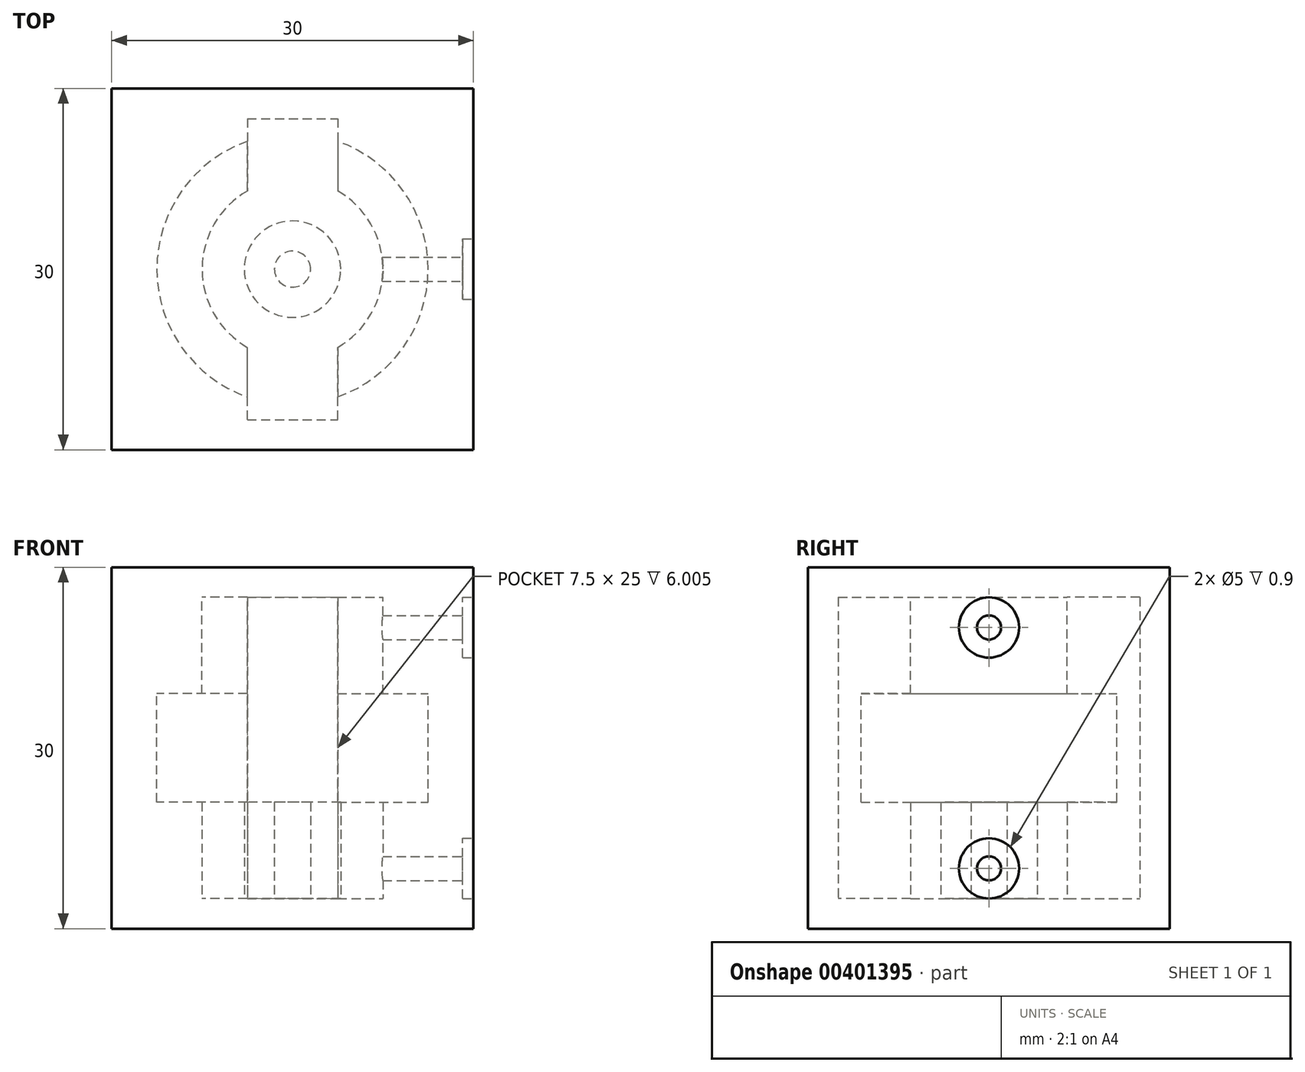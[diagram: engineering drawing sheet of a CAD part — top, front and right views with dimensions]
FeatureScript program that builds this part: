
annotation { "Feature Type Name" : "Feature", "Feature Type Description" : "" }
export const myFeature = defineFeature(function(context is Context, id is Id, definition is map)
    precondition{}
    {
        {
            var Q0;
            Q0=qCreatedBy(makeId("Top.planeOp"),FACE);
            var sketch = newSketch(context, id + "F0", { "sketchPlane" : qUnion([Q0])});
            skLineSegment(sketch, "E0.bottom", {"start": v(-15, 15) * mm, "end": v(15, 15) * mm});
            skLineSegment(sketch, "E0.top", {"start": v(-15, -15) * mm, "end": v(15, -15) * mm});
            skLineSegment(sketch, "E0.left", {"start": v(-15, 15) * mm, "end": v(-15, -15) * mm});
            skLineSegment(sketch, "E0.right", {"start": v(15, 15) * mm, "end": v(15, -15) * mm});
            skSolve(sketch);
        }
        {
            var Q0;
            Q0 = qSketchRegion(id + "F0", true);
            extrude(context, id + "F1", {"entities" : qUnion([Q0]), "depth" : 30 * mm});
        }
        {
            var Q0;
            Q0=makeQuery(id+"F1.opExtrude","CAP_FACE",FACE,{"disambiguationData":[OSD([sQuery(id+"F0.wireOp",EDGE,"E0.bottom"),sQuery(id+"F0.wireOp",EDGE,"E0.top"),sQuery(id+"F0.wireOp",EDGE,"E0.left"),sQuery(id+"F0.wireOp",EDGE,"E0.right")])],"isStart":false});
            var Q1;
            Q1=makeQuery(id+"F1.opExtrude","SWEPT_BODY",BODY,{"disambiguationData":[OSD([sQuery(id+"F0.wireOp",EDGE,"E0.bottom"),sQuery(id+"F0.wireOp",EDGE,"E0.top"),sQuery(id+"F0.wireOp",EDGE,"E0.left"),sQuery(id+"F0.wireOp",EDGE,"E0.right")])]});
            shell(context, id + "F2", {"isHollow" : true, "entities" : qUnion([Q0]), "parts" : qUnion([Q1]), "thickness" : 2.5 * mm});
        }
        {
            var Q0;
            Q0=qCreatedBy(makeId("Top.planeOp"),FACE);
            var sketch = newSketch(context, id + "F3", { "sketchPlane" : qUnion([Q0])});
            skArc(sketch, "E1", {"start": v(7.5, 0) * mm, "mid": v(6.5, 3.75) * mm, "end": v(3.75, 6.5) * mm});
            skLineSegment(sketch, "E2", {"start": v(3.75, 12.5) * mm, "end": v(3.75, 6.5) * mm});
            skLineSegment(sketch, "E3", {"start": v(-3.75, 12.5) * mm, "end": v(-3.75, 6.5) * mm});
            skArc(sketch, "E4.trimOffspring", {"start": v(-3.75, 6.5) * mm, "mid": v(-6.5, 3.75) * mm, "end": v(-7.5, 0) * mm});
            skArc(sketch, "E5.MirrorCS", {"start": v(-3.75, -6.5) * mm, "mid": v(-6.5, -3.75) * mm, "end": v(-7.5, 0) * mm});
            skLineSegment(sketch, "E6.MirrorCS", {"start": v(-3.75, -12.5) * mm, "end": v(-3.75, -6.5) * mm});
            skLineSegment(sketch, "E7.MirrorCS", {"start": v(3.75, -12.5) * mm, "end": v(3.75, -6.5) * mm});
            skArc(sketch, "E8.MirrorCS", {"start": v(7.5, 0) * mm, "mid": v(6.5, -3.75) * mm, "end": v(3.75, -6.5) * mm});
            skPoint(sketch, "E9.MirrorCS.end.orphan", {"position": v(3.75, -12.5) * mm});
            skPoint(sketch, "E9.MirrorCS.start.orphan", {"position": v(-3.75, -12.5) * mm});
            skLineSegment(sketch, "E10.0", {"start": v(-12.5, 12.5) * mm, "end": v(-12.5, -12.5) * mm});
            skLineSegment(sketch, "E11", {"start": v(-12.5, 12.5) * mm, "end": v(-3.75, 12.5) * mm});
            skLineSegment(sketch, "E12", {"start": v(-12.5, -12.5) * mm, "end": v(-3.75, -12.5) * mm});
            skLineSegment(sketch, "E13.0", {"start": v(12.5, 12.5) * mm, "end": v(12.5, -12.5) * mm});
            skLineSegment(sketch, "E14", {"start": v(12.5, 12.5) * mm, "end": v(3.75, 12.5) * mm});
            skLineSegment(sketch, "E15", {"start": v(12.5, -12.5) * mm, "end": v(3.75, -12.5) * mm});
            skSolve(sketch);
        }
        {
            var Q0;
            Q0=makeQuery(id+"F1.opExtrude","CAP_FACE",FACE,{"disambiguationData":[OSD([sQuery(id+"F0.wireOp",EDGE,"E0.bottom"),sQuery(id+"F0.wireOp",EDGE,"E0.top"),sQuery(id+"F0.wireOp",EDGE,"E0.left"),sQuery(id+"F0.wireOp",EDGE,"E0.right")])],"isStart":false});
            var Q1;
            Q1=makeQuery(id+"F1.opExtrude","CAP_FACE",FACE,{"disambiguationData":[OSD([sQuery(id+"F0.wireOp",EDGE,"E0.bottom"),sQuery(id+"F0.wireOp",EDGE,"E0.top"),sQuery(id+"F0.wireOp",EDGE,"E0.left"),sQuery(id+"F0.wireOp",EDGE,"E0.right")])],"isStart":true});
            cPlane(context, id + "F4", {"entities" : qUnion([Q0, Q1]), "cplaneType" : CPlaneType.MID_PLANE, "offset" : 25 * mm, "width" : 150 * mm, "height" : 150 * mm});
        }
        {
            var Q0;
            Q0=qCreatedBy(id+"F4.planeOp",FACE);
            cPlane(context, id + "F5", {"entities" : qUnion([Q0]), "cplaneType" : CPlaneType.OFFSET, "offset" : (9 / 2) * mm, "oppositeDirection" : true, "width" : 150 * mm, "height" : 150 * mm});
        }
        {
            var Q0;
            Q0 = qSketchRegion(id + "F3", true);
            var Q1;
            Q1=qCreatedBy(id+"F5.planeOp",FACE);
            extrude(context, id + "F6", {"entities" : qUnion([Q0]), "operationType" : NewBodyOperationType.ADD, "endBound" : BoundingType.UP_TO_SURFACE, "endBoundEntityFace" : qUnion([Q1]), "depth" : 25 * mm});
        }
        {
            var Q0;
            Q0=makeQuery(id+"F1.opExtrude","CAP_FACE",FACE,{"disambiguationData":[OSD([sQuery(id+"F0.wireOp",EDGE,"E0.bottom"),sQuery(id+"F0.wireOp",EDGE,"E0.top"),sQuery(id+"F0.wireOp",EDGE,"E0.left"),sQuery(id+"F0.wireOp",EDGE,"E0.right")])],"isStart":false});
            var sketch = newSketch(context, id + "F7", { "sketchPlane" : qUnion([Q0])});
            skArc(sketch, "E16", {"start": v(7.5, 0) * mm, "mid": v(6.5, 3.75) * mm, "end": v(3.75, 6.5) * mm});
            skLineSegment(sketch, "E17", {"start": v(3.75, 12.5) * mm, "end": v(3.75, 6.5) * mm});
            skLineSegment(sketch, "E18", {"start": v(-3.75, 12.5) * mm, "end": v(-3.75, 6.5) * mm});
            skArc(sketch, "E19.trimOffspring", {"start": v(-3.75, 6.5) * mm, "mid": v(-6.5, 3.75) * mm, "end": v(-7.5, 0) * mm});
            skArc(sketch, "E20.MirrorCS", {"start": v(-3.75, -6.5) * mm, "mid": v(-6.5, -3.75) * mm, "end": v(-7.5, 0) * mm});
            skLineSegment(sketch, "E21.MirrorCS", {"start": v(-3.75, -12.5) * mm, "end": v(-3.75, -6.5) * mm});
            skLineSegment(sketch, "E22.MirrorCS", {"start": v(3.75, -12.5) * mm, "end": v(3.75, -6.5) * mm});
            skArc(sketch, "E23.MirrorCS", {"start": v(7.5, 0) * mm, "mid": v(6.5, -3.75) * mm, "end": v(3.75, -6.5) * mm});
            skPoint(sketch, "E24.MirrorCS.end.orphan", {"position": v(3.75, -12.5) * mm});
            skPoint(sketch, "E24.MirrorCS.start.orphan", {"position": v(-3.75, -12.5) * mm});
            skLineSegment(sketch, "E25.0", {"start": v(-12.5, 12.5) * mm, "end": v(-12.5, -12.5) * mm});
            skLineSegment(sketch, "E26", {"start": v(-12.5, 12.5) * mm, "end": v(-3.75, 12.5) * mm});
            skLineSegment(sketch, "E27", {"start": v(-12.5, -12.5) * mm, "end": v(-3.75, -12.5) * mm});
            skLineSegment(sketch, "E28.0", {"start": v(12.5, 12.5) * mm, "end": v(12.5, -12.5) * mm});
            skLineSegment(sketch, "E29", {"start": v(12.5, 12.5) * mm, "end": v(3.75, 12.5) * mm});
            skLineSegment(sketch, "E30", {"start": v(12.5, -12.5) * mm, "end": v(3.75, -12.5) * mm});
            skSolve(sketch);
        }
        {
            var Q0;
            Q0=qCreatedBy(id+"F4.planeOp",FACE);
            cPlane(context, id + "F8", {"entities" : qUnion([Q0]), "cplaneType" : CPlaneType.OFFSET, "offset" : (9 / 2) * mm, "width" : 150 * mm, "height" : 150 * mm});
        }
        {
            var Q0;
            Q0 = qSketchRegion(id + "F7", true);
            var Q1;
            Q1=qCreatedBy(id+"F8.planeOp",FACE);
            extrude(context, id + "F9", {"entities" : qUnion([Q0]), "operationType" : NewBodyOperationType.ADD, "endBound" : BoundingType.UP_TO_SURFACE, "oppositeDirection" : true, "endBoundEntityFace" : qUnion([Q1]), "depth" : 25 * mm});
        }
        {
            var Q0;
            Q0=qCreatedBy(id+"F4.planeOp",FACE);
            var sketch = newSketch(context, id + "F10", { "sketchPlane" : qUnion([Q0])});
            skLineSegment(sketch, "E31.0", {"start": v(3.75, -12.5) * mm, "end": v(3.75, -10.6) * mm});
            skLineSegment(sketch, "E32.0", {"start": v(3.75, -12.5) * mm, "end": v(12.5, -12.5) * mm});
            skLineSegment(sketch, "E33.0", {"start": v(12.5, -12.5) * mm, "end": v(12.5, 12.5) * mm});
            skPoint(sketch, "E34.0", {"position": v(8.12, 12.5) * mm});
            skLineSegment(sketch, "E35.0", {"start": v(3.75, 12.5) * mm, "end": v(3.75, 10.6) * mm});
            skLineSegment(sketch, "E36.0", {"start": v(-3.75, 12.5) * mm, "end": v(-3.75, 10.6) * mm});
            skLineSegment(sketch, "E37.0", {"start": v(-3.75, 12.5) * mm, "end": v(-12.5, 12.5) * mm});
            skLineSegment(sketch, "E38.0", {"start": v(-12.5, -12.5) * mm, "end": v(-12.5, 12.5) * mm});
            skLineSegment(sketch, "E39.0", {"start": v(-3.75, -12.5) * mm, "end": v(-12.5, -12.5) * mm});
            skLineSegment(sketch, "E40.0", {"start": v(-3.75, -12.5) * mm, "end": v(-3.75, -10.6) * mm});
            skArc(sketch, "E41", {"start": v(3.75, -10.6) * mm, "mid": v(11.25, 0) * mm, "end": v(3.75, 10.6) * mm});
            skPoint(sketch, "E42.orphan", {"position": v(3.75, -6.5) * mm});
            skPoint(sketch, "E43.orphan", {"position": v(-3.75, -6.5) * mm});
            skPoint(sketch, "E44.orphan", {"position": v(-3.75, 6.5) * mm});
            skPoint(sketch, "E45.orphan", {"position": v(3.75, 6.5) * mm});
            skArc(sketch, "E46.trimOffspring", {"start": v(-3.75, 10.6) * mm, "mid": v(-11.25, 0) * mm, "end": v(-3.75, -10.6) * mm});
            skLineSegment(sketch, "E47", {"start": v(3.75, 12.5) * mm, "end": v(12.5, 12.5) * mm});
            skSolve(sketch);
        }
        {
            var Q0;
            Q0 = qSketchRegion(id + "F10", true);
            extrude(context, id + "F11", {"entities" : qUnion([Q0]), "operationType" : NewBodyOperationType.ADD, "endBound" : BoundingType.UP_TO_NEXT, "oppositeDirection" : true, "depth" : 30 * mm});
        }
        {
            var Q0;
            Q0 = qSketchRegion(id + "F10", true);
            extrude(context, id + "F12", {"entities" : qUnion([Q0]), "operationType" : NewBodyOperationType.ADD, "endBound" : BoundingType.UP_TO_NEXT, "depth" : 25 * mm});
        }
        {
            var Q0;
            Q0=makeQuery(id+"F1.opExtrude","SWEPT_FACE",FACE,{"disambiguationData":[OSD([sQuery(id+"F0.wireOp",EDGE,"E0.right")])]});
            var sketch = newSketch(context, id + "F13", { "sketchPlane" : qUnion([Q0])});
            skPoint(sketch, "E48", {"position": v(0, 5) * mm});
            skPoint(sketch, "E49.MirrorP", {"position": v(0, 25) * mm});
            skSolve(sketch);
        }
        {
            var Q0;
            Q0=sQuery(id+"F13.wireOp",VERTEX,"E48");
            var Q1;
            Q1=sQuery(id+"F13.wireOp",VERTEX,"E49.MirrorP");
            var Q2;
            Q2=makeQuery(id+"F1.opExtrude","SWEPT_BODY",BODY,{"disambiguationData":[OSD([sQuery(id+"F0.wireOp",EDGE,"E0.bottom"),sQuery(id+"F0.wireOp",EDGE,"E0.top"),sQuery(id+"F0.wireOp",EDGE,"E0.left"),sQuery(id+"F0.wireOp",EDGE,"E0.right")])]});
            hole(context, id + "F14", {"style" : HoleStyle.C_BORE, "endStyle" : HoleEndStyle.BLIND, "holeDiameter" : 2 * mm, "cBoreDiameter" : 5 * mm, "cBoreDepth" : .9 * mm, "holeDepth" : 15 * mm, "isTappedThrough" : true, "tappedDepth" : 12 * mm, "tapClearance" : 3, "locations" : qUnion([Q0, Q1]), "scope" : qUnion([Q2])});
        }
        {
            var Q0;
            Q0=qCreatedBy(makeId("Top.planeOp"),FACE);
            var sketch = newSketch(context, id + "F15", { "sketchPlane" : qUnion([Q0])});
            skCircle(sketch, "E50", {"center": v(0, 0) * mm, "radius": 4 * mm});
            skCircle(sketch, "E51", {"center": v(0, 0) * mm, "radius": 1.5 * mm});
            skSolve(sketch);
        }
        {
            var Q0;
            Q0 = qSketchRegion(id + "F15", true);
            var Q1;
            Q1=qCreatedBy(id+"F5.planeOp",FACE);
            extrude(context, id + "F16", {"entities" : qUnion([Q0]), "operationType" : NewBodyOperationType.ADD, "endBound" : BoundingType.UP_TO_SURFACE, "endBoundEntityFace" : qUnion([Q1]), "depth" : 15 * mm});
        }
    });
